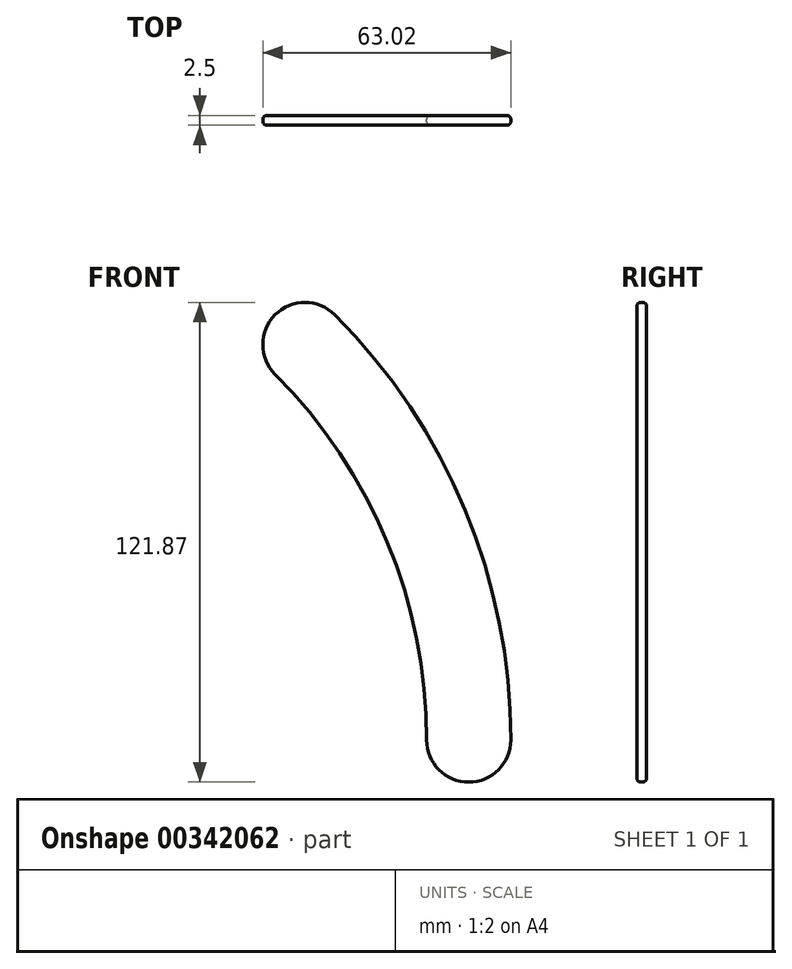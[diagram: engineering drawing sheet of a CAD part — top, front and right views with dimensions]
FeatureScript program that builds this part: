
annotation { "Feature Type Name" : "Feature", "Feature Type Description" : "" }
export const myFeature = defineFeature(function(context is Context, id is Id, definition is map)
    precondition{}
    {
        {
            var Q0;
            Q0=qCreatedBy(makeId("Front.planeOp"),FACE);
            var sketch = newSketch(context, id + "F0", { "sketchPlane" : qUnion([Q0])});
            skArc(sketch, "E0", {"start": v(152.8, 0) * mm, "mid": v(141.16, 58.47) * mm, "end": v(108.04, 108.04) * mm});
            skArc(sketch, "E1", {"start": v(131.4, 0) * mm, "mid": v(121.39, 50.28) * mm, "end": v(92.9, 92.9) * mm});
            skLineSegment(sketch, "E2", {"start": v(0, 0) * mm, "end": v(152.8, 0) * mm, "construction": true});
            skLineSegment(sketch, "E3", {"start": v(0, 0) * mm, "end": v(108.04, 108.04) * mm, "construction": true});
            skPoint(sketch, "E4", {"position": v(92.9, 92.9) * mm});
            skPoint(sketch, "E5", {"position": v(108.04, 108.04) * mm});
            skPoint(sketch, "E6", {"position": v(131.4, 0) * mm});
            skPoint(sketch, "E7", {"position": v(152.8, 0) * mm});
            skArc(sketch, "E8", {"start": v(108.04, 108.04) * mm, "mid": v(92.9, 108.04) * mm, "end": v(92.9, 92.9) * mm});
            skArc(sketch, "E9", {"start": v(131.4, 0) * mm, "mid": v(142.1, -10.7) * mm, "end": v(152.79, 0) * mm});
            skCircle(sketch, "E10", {"center": v(0, 0) * mm, "radius": 148.23 * mm, "construction": true});
            skCircle(sketch, "E11", {"center": v(0, 0) * mm, "radius": 135.95 * mm, "construction": true});
            skSolve(sketch);
        }
        {
            var Q0;
            Q0 = qSketchRegion(id + "F0", true);
            extrude(context, id + "F1", {"entities" : qUnion([Q0]), "depth" : 2.5 * mm});
        }
        {
            var Q0;
            Q0=makeQuery(id+"F1.opExtrude","CAP_EDGE",EDGE,{"disambiguationData":[OSD([sQuery(id+"F0.wireOp",EDGE,"E0")])],"isStart":false});
            var Q1;
            Q1=makeQuery(id+"F1.opExtrude","CAP_EDGE",EDGE,{"disambiguationData":[OSD([sQuery(id+"F0.wireOp",EDGE,"E0")])],"isStart":true});
            fillet(context, id + "F2", {"entities" : qUnion([Q0, Q1]), "radius" : 1 * mm, "tangentPropagation" : true, "allowEdgeOverflow" : false});
        }
    });
